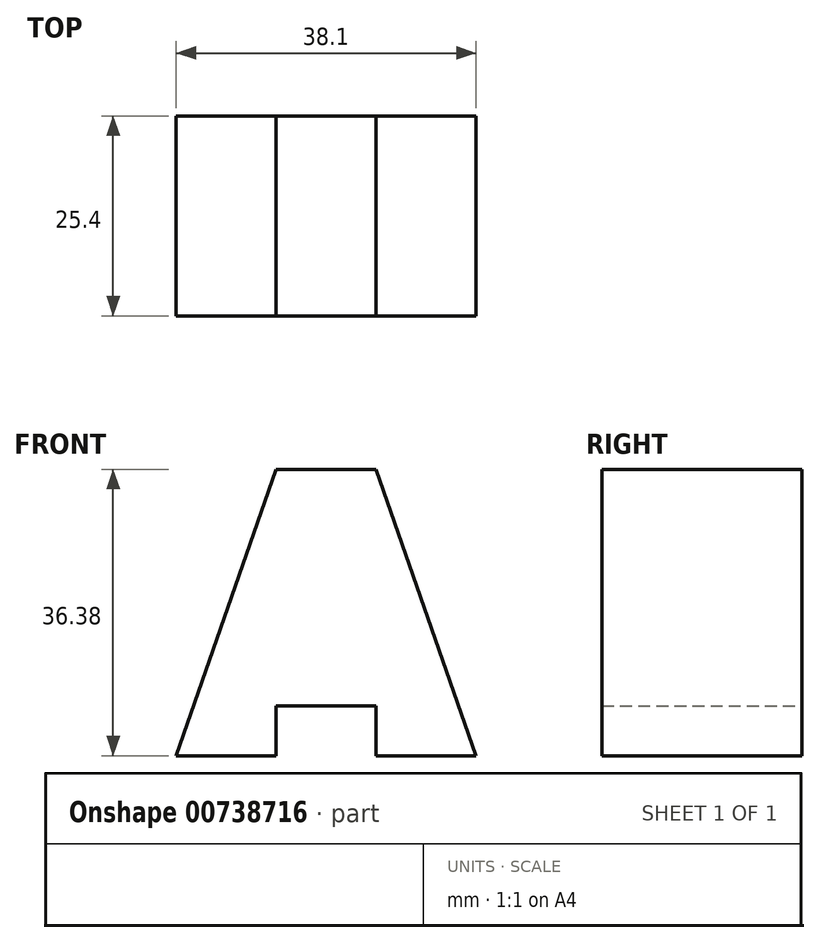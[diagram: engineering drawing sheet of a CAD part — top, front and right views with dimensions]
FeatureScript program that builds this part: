
annotation { "Feature Type Name" : "Feature", "Feature Type Description" : "" }
export const myFeature = defineFeature(function(context is Context, id is Id, definition is map)
    precondition{}
    {
        {
            var Q0;
            Q0=qCreatedBy(makeId("Front.planeOp"),FACE);
            var sketch = newSketch(context, id + "F0", { "sketchPlane" : qUnion([Q0])});
            skLineSegment(sketch, "E0", {"start": v(0, 0) * mm, "end": v(12.7, 36.38) * mm});
            skLineSegment(sketch, "E1", {"start": v(12.7, 36.38) * mm, "end": v(25.4, 36.38) * mm});
            skLineSegment(sketch, "E2", {"start": v(25.4, 36.38) * mm, "end": v(38.1, 0) * mm});
            skLineSegment(sketch, "E3", {"start": v(38.1, 0) * mm, "end": v(25.4, 0) * mm});
            skLineSegment(sketch, "E4", {"start": v(25.4, 0) * mm, "end": v(25.4, 6.35) * mm});
            skLineSegment(sketch, "E5", {"start": v(25.4, 6.35) * mm, "end": v(12.7, 6.35) * mm});
            skLineSegment(sketch, "E6", {"start": v(12.7, 6.35) * mm, "end": v(12.7, 0) * mm});
            skLineSegment(sketch, "E7", {"start": v(12.7, 0) * mm, "end": v(0, 0) * mm});
            skSolve(sketch);
        }
        {
            var Q0;
            Q0 = qSketchRegion(id + "F0", true);
            extrude(context, id + "F1", {"entities" : qUnion([Q0]), "depth" : 25.4 * mm, "offsetDistance" : 25.4 * mm});
        }
    });
